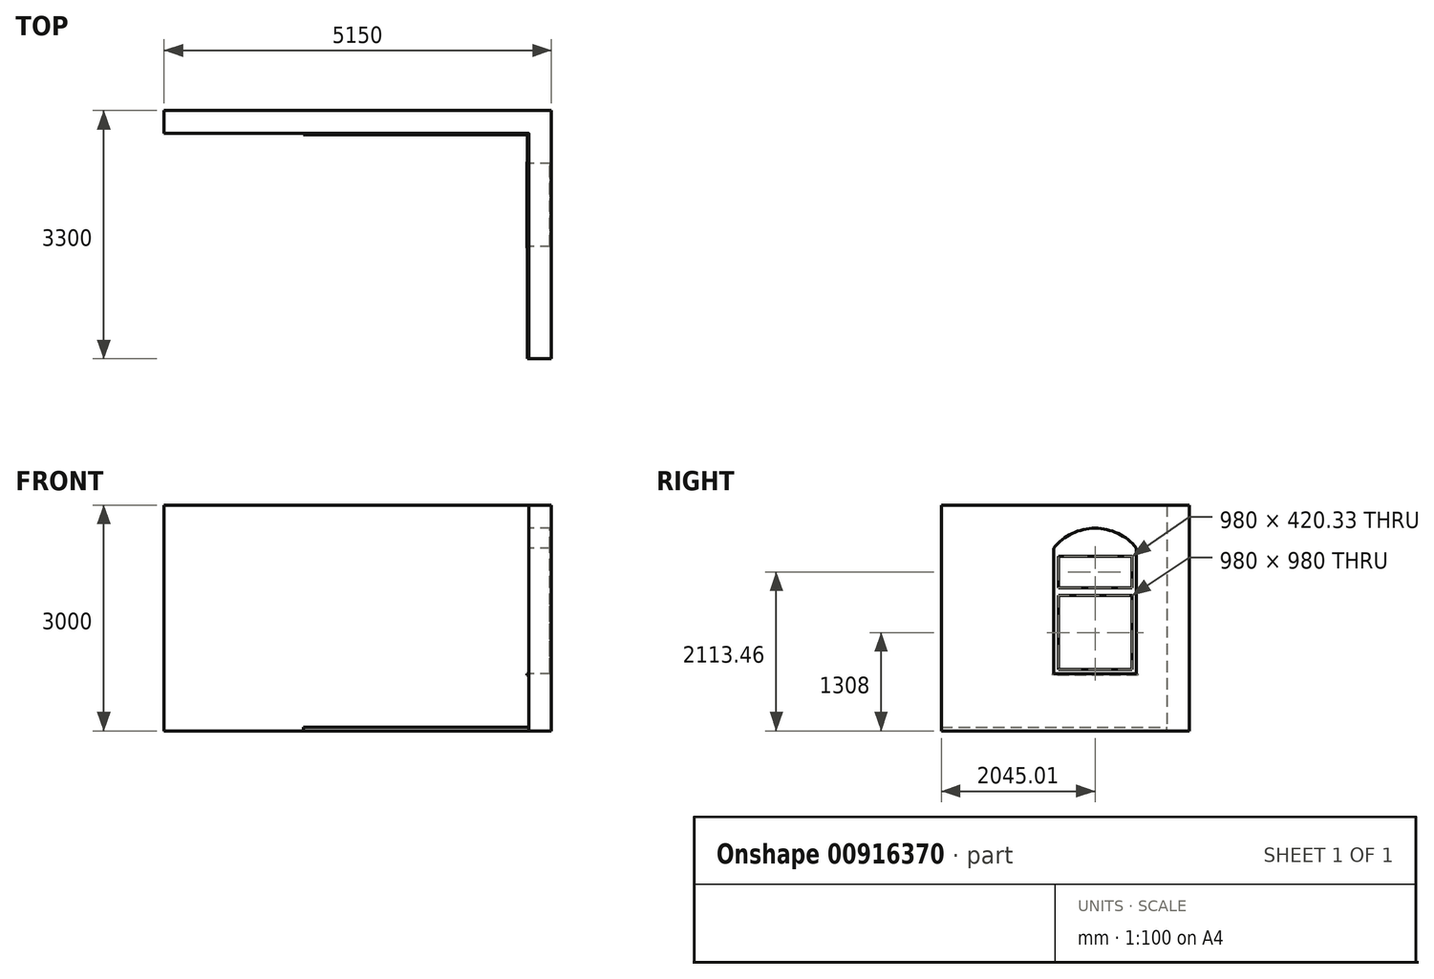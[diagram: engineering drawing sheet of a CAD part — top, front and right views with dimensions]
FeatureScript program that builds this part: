
annotation { "Feature Type Name" : "Feature", "Feature Type Description" : "" }
export const myFeature = defineFeature(function(context is Context, id is Id, definition is map)
    precondition{}
    {
        {
            var Q0;
            Q0=qCreatedBy(makeId("Top.planeOp"),FACE);
            var sketch = newSketch(context, id + "F0", { "sketchPlane" : qUnion([Q0])});
            skLineSegment(sketch, "E0.bottom", {"start": v(-2543.38, 1492.05) * mm, "end": v(2306.62, 1492.05) * mm});
            skLineSegment(sketch, "E0.top", {"start": v(-2543.38, 1192.05) * mm, "end": v(2306.62, 1192.05) * mm});
            skLineSegment(sketch, "E0.left", {"start": v(-2543.38, 1492.05) * mm, "end": v(-2543.38, 1192.05) * mm});
            skLineSegment(sketch, "E0.right", {"start": v(2306.62, 1492.05) * mm, "end": v(2306.62, 1192.05) * mm});
            skLineSegment(sketch, "E1.bottom", {"start": v(2306.62, 1492.05) * mm, "end": v(2606.62, 1492.05) * mm});
            skLineSegment(sketch, "E1.top", {"start": v(2306.62, -1807.95) * mm, "end": v(2606.62, -1807.95) * mm});
            skLineSegment(sketch, "E1.left", {"start": v(2306.62, 1492.05) * mm, "end": v(2306.62, -1807.95) * mm});
            skLineSegment(sketch, "E1.right", {"start": v(2606.62, 1492.05) * mm, "end": v(2606.62, -1807.95) * mm});
            skSolve(sketch);
        }
        {
            var Q0;
            {var subQ0=sQuery(id+"F0.wireOp",EDGE,"E0.bottom");Q0=makeQuery(id+"F0.imprint","IMPRINT",FACE,{"disambiguationData":[TD([[makeQuery(id+"F0.imprint","IMPRINT",EDGE,{"derivedFrom":subQ0}),-1.0]])]});}
            var Q1;
            {var subQ3=sQuery(id+"F0.wireOp",EDGE,"E1.bottom");Q1=makeQuery(id+"F0.imprint","IMPRINT",FACE,{"disambiguationData":[TD([[makeQuery(id+"F0.imprint","IMPRINT",EDGE,{"derivedFrom":subQ3}),-1.0]])]});}
            extrude(context, id + "F1", {"entities" : qUnion([Q0, Q1]), "depth" : 3000 * mm, "offsetDistance" : 25 * mm});
        }
        {
            var Q0;
            Q0=makeQuery(id+"F1.opExtrude","SWEPT_FACE",FACE,{"disambiguationData":[OSD([sQuery(id+"F0.wireOp",EDGE,"E1.left")])]});
            var sketch = newSketch(context, id + "F2", { "sketchPlane" : qUnion([Q0])});
            skLineSegment(sketch, "E2.bottom", {"start": v(-787.05, 758) * mm, "end": v(312.95, 758) * mm});
            skLineSegment(sketch, "E2.top", {"start": v(-787.05, 2431.72) * mm, "end": v(312.95, 2431.72) * mm});
            skLineSegment(sketch, "E2.left", {"start": v(-787.05, 758) * mm, "end": v(-787.05, 2431.72) * mm});
            skLineSegment(sketch, "E2.right", {"start": v(312.95, 758) * mm, "end": v(312.95, 2431.72) * mm});
            skArc(sketch, "E3", {"start": v(312.95, 2431.72) * mm, "mid": v(-237.05, 2694.28) * mm, "end": v(-787.05, 2431.72) * mm});
            skLineSegment(sketch, "E4.bottom", {"start": v(-807.05, 758) * mm, "end": v(332.95, 758) * mm});
            skLineSegment(sketch, "E4.top", {"start": v(-807.05, 738) * mm, "end": v(332.95, 738) * mm});
            skLineSegment(sketch, "E4.left", {"start": v(-807.05, 758) * mm, "end": v(-807.05, 738) * mm});
            skLineSegment(sketch, "E4.right", {"start": v(332.95, 758) * mm, "end": v(332.95, 738) * mm});
            skPoint(sketch, "E5", {"position": v(-237.05, 748) * mm});
            skPoint(sketch, "E5.positionSnap0", {"position": v(332.95, 748) * mm});
            skPoint(sketch, "E5.positionSnap1", {"position": v(-237.05, 738) * mm});
            skPoint(sketch, "E6", {"position": v(312.95, 1594.86) * mm});
            skLineSegment(sketch, "E7.bottom", {"start": v(-727.05, 818) * mm, "end": v(252.95, 818) * mm});
            skLineSegment(sketch, "E7.top", {"start": v(-727.05, 1798) * mm, "end": v(252.95, 1798) * mm});
            skLineSegment(sketch, "E7.left", {"start": v(-727.05, 818) * mm, "end": v(-727.05, 1798) * mm});
            skLineSegment(sketch, "E7.right", {"start": v(252.95, 818) * mm, "end": v(252.95, 1798) * mm});
            skLineSegment(sketch, "E8.bottom", {"start": v(-727.05, 1903.3) * mm, "end": v(252.95, 1903.3) * mm});
            skLineSegment(sketch, "E8.top", {"start": v(-727.05, 2323.62) * mm, "end": v(252.95, 2323.62) * mm});
            skLineSegment(sketch, "E8.left", {"start": v(-727.05, 1903.3) * mm, "end": v(-727.05, 2323.62) * mm});
            skLineSegment(sketch, "E8.right", {"start": v(252.95, 1903.3) * mm, "end": v(252.95, 2323.62) * mm});
            skSolve(sketch);
        }
        {
            var Q0;
            Q0=makeQuery(id+"F2.imprint","IMPRINT",FACE,{"disambiguationData":[TD([[makeQuery(id+"F2.imprint","IMPRINT",EDGE,{"derivedFrom":sQuery(id+"F2.wireOp",EDGE,"E2.top")}),-1.0]])]});
            var Q1;
            Q1=makeQuery(id+"F2.imprint","IMPRINT",FACE,{"disambiguationData":[TD([[makeQuery(id+"F2.imprint","IMPRINT",EDGE,{"derivedFrom":sQuery(id+"F2.wireOp",EDGE,"E2.top")}),1.0]])]});
            extrude(context, id + "F3", {"entities" : qUnion([Q0, Q1]), "operationType" : NewBodyOperationType.REMOVE, "oppositeDirection" : true, "depth" : 300 * mm, "offsetDistance" : 25 * mm});
        }
        {
            var Q0;
            Q0=makeQuery(id+"F2.imprint","IMPRINT",FACE,{"disambiguationData":[TD([[makeQuery(id+"F2.imprint","IMPRINT",EDGE,{"derivedFrom":sQuery(id+"F2.wireOp",EDGE,"E4.top")}),1.0]])]});
            extrude(context, id + "F4", {"entities" : qUnion([Q0]), "operationType" : NewBodyOperationType.ADD, "depth" : 25 * mm, "offsetDistance" : 25 * mm});
        }
        {
            var Q0;
            Q0=makeQuery(id+"F2.imprint","IMPRINT",FACE,{"disambiguationData":[TD([[makeQuery(id+"F2.imprint","IMPRINT",EDGE,{"derivedFrom":sQuery(id+"F2.wireOp",EDGE,"E8.bottom")}),1.0]])]});
            var Q1;
            Q1=makeQuery(id+"F2.imprint","IMPRINT",FACE,{"disambiguationData":[TD([[makeQuery(id+"F2.imprint","IMPRINT",EDGE,{"derivedFrom":sQuery(id+"F2.wireOp",EDGE,"E7.bottom")}),1.0]])]});
            extrude(context, id + "F5", {"entities" : qUnion([Q0, Q1]), "operationType" : NewBodyOperationType.REMOVE, "oppositeDirection" : true, "depth" : 280 * mm, "offsetDistance" : 25 * mm});
        }
        {
            var Q0;
            Q0=makeQuery(id+"F2.imprint","IMPRINT",FACE,{"disambiguationData":[TD([[makeQuery(id+"F2.imprint","IMPRINT",EDGE,{"derivedFrom":sQuery(id+"F2.wireOp",EDGE,"E2.top")}),-1.0]])]});
            var Q1;
            Q1=makeQuery(id+"F2.imprint","IMPRINT",FACE,{"disambiguationData":[TD([[makeQuery(id+"F2.imprint","IMPRINT",EDGE,{"derivedFrom":sQuery(id+"F2.wireOp",EDGE,"E2.top")}),1.0]])]});
            extrude(context, id + "F6", {"entities" : qUnion([Q0, Q1]), "oppositeDirection" : true, "depth" : 300 * mm, "offsetDistance" : 25 * mm, "hasSecondDirection" : true, "secondDirectionOppositeDirection" : true, "secondDirectionDepth" : 280 * mm});
        }
        {
            var Q0;
            Q0=makeQuery(id+"F1.opExtrude","SWEPT_FACE",FACE,{"disambiguationData":[OSD([sQuery(id+"F0.wireOp",EDGE,"E0.top")])]});
            var sketch = newSketch(context, id + "F7", { "sketchPlane" : qUnion([Q0])});
            skPoint(sketch, "E9", {"position": v(936.62, 0) * mm});
            skLineSegment(sketch, "E10.bottom", {"start": v(2306.62, 0) * mm, "end": v(2286.62, 0) * mm});
            skLineSegment(sketch, "E10.left", {"start": v(2306.62, 0) * mm, "end": v(2306.62, 50) * mm});
            skFitSpline(sketch, "E11", {"points": [v(2286.62, 0) * mm, v(2306.62, 50) * mm], "startDerivative": vector(84.56, 0) * mm, "endDerivative": vector(20, 50) * mm});
            skSolve(sketch);
        }
        {
            var Q0;
            Q0=makeQuery(id+"F7.imprint","IMPRINT",FACE,{"disambiguationData":[TD([[makeQuery(id+"F7.imprint","IMPRINT",EDGE,{"derivedFrom":sQuery(id+"F7.wireOp",EDGE,"E10.bottom")}),1.0]])]});
            var Q1;
            Q1 = qConstructionFilter(qBodyType(qCreatedBy(id + "F7" ,EDGE), BodyType.WIRE), ConstructionObject.NO);
            extrude(context, id + "F8", {"entities" : qUnion([Q0]), "surfaceOperationType" : NewSurfaceOperationType.ADD, "surfaceEntities" : qUnion([Q1]), "depth" : 3000 * mm, "offsetDistance" : 25 * mm});
        }
        {
            var Q0;
            Q0=makeQuery(id+"F8.opExtrude","SWEPT_BODY",BODY,{"disambiguationData":[OSD([sQuery(id+"F7.wireOp",EDGE,"E10.bottom"),sQuery(id+"F7.wireOp",EDGE,"E10.left"),sQuery(id+"F7.wireOp",EDGE,"E11")])]});
            var Q1;
            Q1=makeQuery(id+"F1.opExtrude","SWEPT_EDGE",EDGE,{"disambiguationData":[OSD([sQuery(id+"F0.wireOp",EDGE,"E0.top"),sQuery(id+"F0.wireOp",EDGE,"E1.left")])]});
            transform(context, id + "F9", {"entities" : qUnion([Q0]), "transformType" : TransformType.ROTATION, "transformAxis" : qUnion([Q1]), "angle" : 90 * degree, "makeCopy" : true});
        }
        {
            var Q0;
            Q0=makeQuery(id+"F9.opPattern","COPY",BODY,{"derivedFrom":makeQuery(id+"F8.opExtrude","SWEPT_BODY",BODY,{"disambiguationData":[OSD([sQuery(id+"F7.wireOp",EDGE,"E10.bottom"),sQuery(id+"F7.wireOp",EDGE,"E10.left"),sQuery(id+"F7.wireOp",EDGE,"E11")])]}),"instanceName":"1"});
            var Q1;
            Q1=makeQuery(id+"F1.opExtrude","SWEPT_FACE",FACE,{"disambiguationData":[OSD([sQuery(id+"F0.wireOp",EDGE,"E0.top")])]});
            mirror(context, id + "F10", {"operationType" : NewBodyOperationType.ADD, "entities" : qUnion([Q0]), "mirrorPlane" : qUnion([Q1])});
        }
    });
